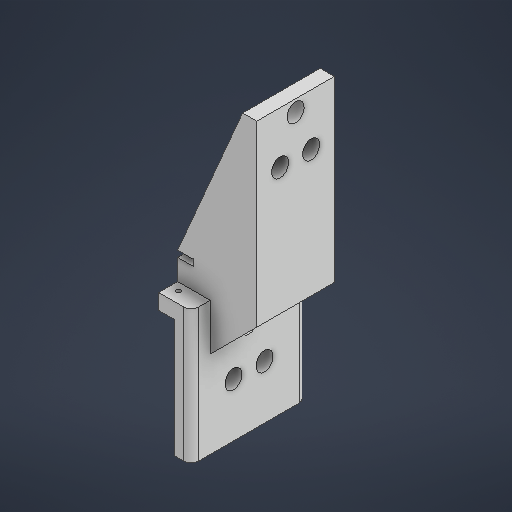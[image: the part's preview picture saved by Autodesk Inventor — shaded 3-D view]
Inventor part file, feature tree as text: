
AUTODESK INVENTOR PART (.ipt)
format: ipt  version: 2025 (Build 290162000, 162)  size: 347,136 bytes
history: native  units: in
note: dims shown in document units (in); Inventor stores cm internally (conversion verified against a paired STEP export)
features: extrude x13, sketch x10, plane x5, chamfer x2, fillet x1
ambient origin geometry x8: Origin, YZ Plane, XZ Plane, XY Plane, X Axis, Y Axis, Z Axis, Center Point
bodies: Solid1 (feature_tree)
feature tree (31):
  sketch  "Sketch1"  dims[d0=0.4331in d1=2.9331in]
  extrude  "Extrusion1"  Depth=2.9331in
  extrude  "Extrusion2"  Depth=0.2854in
  extrude  "Extrusion3"  Depth=0.3937in TaperAngle=0.0deg
  plane  "Work Plane1"
  plane  "Work Plane3"
  sketch  "Sketch4"  dims[d9=0.4213in d10=2.9921in d11=0.0in]
  extrude  "Extrusion4"  Depth=2.9921in TaperAngle=0.0deg
  extrude  "Extrusion11"  Depth=0.1575in
  extrude  "Extrusion6"  Depth=0.1575in
  extrude  "Extrusion7"  Depth=0.3937in
  extrude  "Extrusion8"  Depth=2.1691in
  chamfer  "Chamfer1"  [1 undecoded]
  sketch  "Sketch6"  dims[d14=0.4331in d15=0.1575in d16=0.4331in]
  extrude  "Extrusion9"  Depth=4.9213in TaperAngle=0.0deg
  chamfer  "Chamfer2"  Distance=1.5748in
  extrude  "Extrusion12"  Depth=1.9685in
  plane  "Work Plane4"
  extrude  "Extrusion13"  TaperAngle=0.0deg  [1 undecoded]
  plane  "Work Plane5"
  plane  "Work Plane6"
  extrude  "Extrusion14"  Depth=1.1811in
  extrude  "Extrusion15"  Depth=0.1969in
  fillet  "Fillet1"  Radius=1.0207in
  sketch  "Sketch2"  dims[d2=0.1181in d3=0.2854in]
  sketch  "Sketch3"  dims[d5=0.3937in d6=0.0in d7=0.3937in d8=0.0in]
  sketch  "Sketch5"  dims[d12=1.0668in d13=0.1575in]
  sketch  "Sketch8"  dims[d19=0.3937in d20=0.9331in]
  sketch  "Sketch9"  dims[d21=0.5906in d22=0.0in d23=2.1691in d26=0.0in d27=0.0in]
  sketch  "Sketch10"  dims[d28=1.9685in d29=4.9213in d30=0.0in d31=1.5748in d32=0.0in]
  sketch  "Sketch11"  dims[d33=1.5748in d34=0.0787in d35=0.1598in d36=0.1575in d37=0.4331in d38=0.1575in d39=0.4331in d40=0.3937in d41=0.9331in d44=1.9685in d46=0.0in d47=0.0in d51=1.1811in d52=1.1811in d53=0.7782in d56=0.1969in d57=1.0207in d58=0.0in d59=1.9685in d60=0.8937in d61=0.0in d62=-1.378in d63=0.4331in d64=0.4331in d65=0.4331in d66=1.1393in d67=0.0in d68=0.0in d69=90.0deg d70=1.9685in d71=0.5906in d72=2.7756in d73=2.1393in d74=0.0in d75=0.0in d76=0.3937in d77=0.1575in d78=2.7756in d79=0.0in d80=0.1969in]
note: 2 required parameter values undecoded (feature->parameter linkage not recoverable at this tier; creation-order binding heuristic only, values carry confidence <= 0.55)
